# Revit family: S-754
name_source: partatom
category: Plumbing Fixtures
revit_build: Autodesk Revit 2015 (Build: 20140606_1530(x64)
units: mm (PartAtom-declared; Revit-internal decimal feet)

## types (6) — shared parameters
B = 52 mm
Description = CHANNEL GRID, SQUARE, FOR CHANNELS WIDTH 50
Grid = INOX AISI304
Manufacturer = Jimten
Material = INOX AISI304
Model = S-754
Type Comments = COMPATIBLE WITH VISIBLE OR THIN FRAMES
URL = http://www.jimten.com
zero-valued in all types: Cost

## per-type parameters (varying)
| type | A | N_MatrizHuecos | Reference | Size |
| 50x350mm_SQUARE | 340 mm  [stored 1.11549 ft] | 4 | 13537 | 350mm x 50mm |
| 50x550mm_SQUARE | 540 mm | 6 | 13557 | 550mm x 50mm |
| 50x650mm_SQUARE | 640 mm  [stored 2.09974 ft] | 7 | 13567 | 650mm x 50mm |
| 50x750mm_SQUARE | 740 mm | 8 | 13577 | 750mm x 50mm |
| 50x850mm_SQUARE | 840 mm | 9 | 13587 | 850mm x 50mm |
| 50x950mm_SQUARE | 940 mm | 10 | 13597 | 950mm x 50mm |

note: [stored X ft] marks values corroborated as IEEE doubles in the binary element streams (Revit-internal decimal feet)

## geometry (parser evidence)
native form markers: Blend x6, Sweep x2
no freeform markers — native parametric forms only
